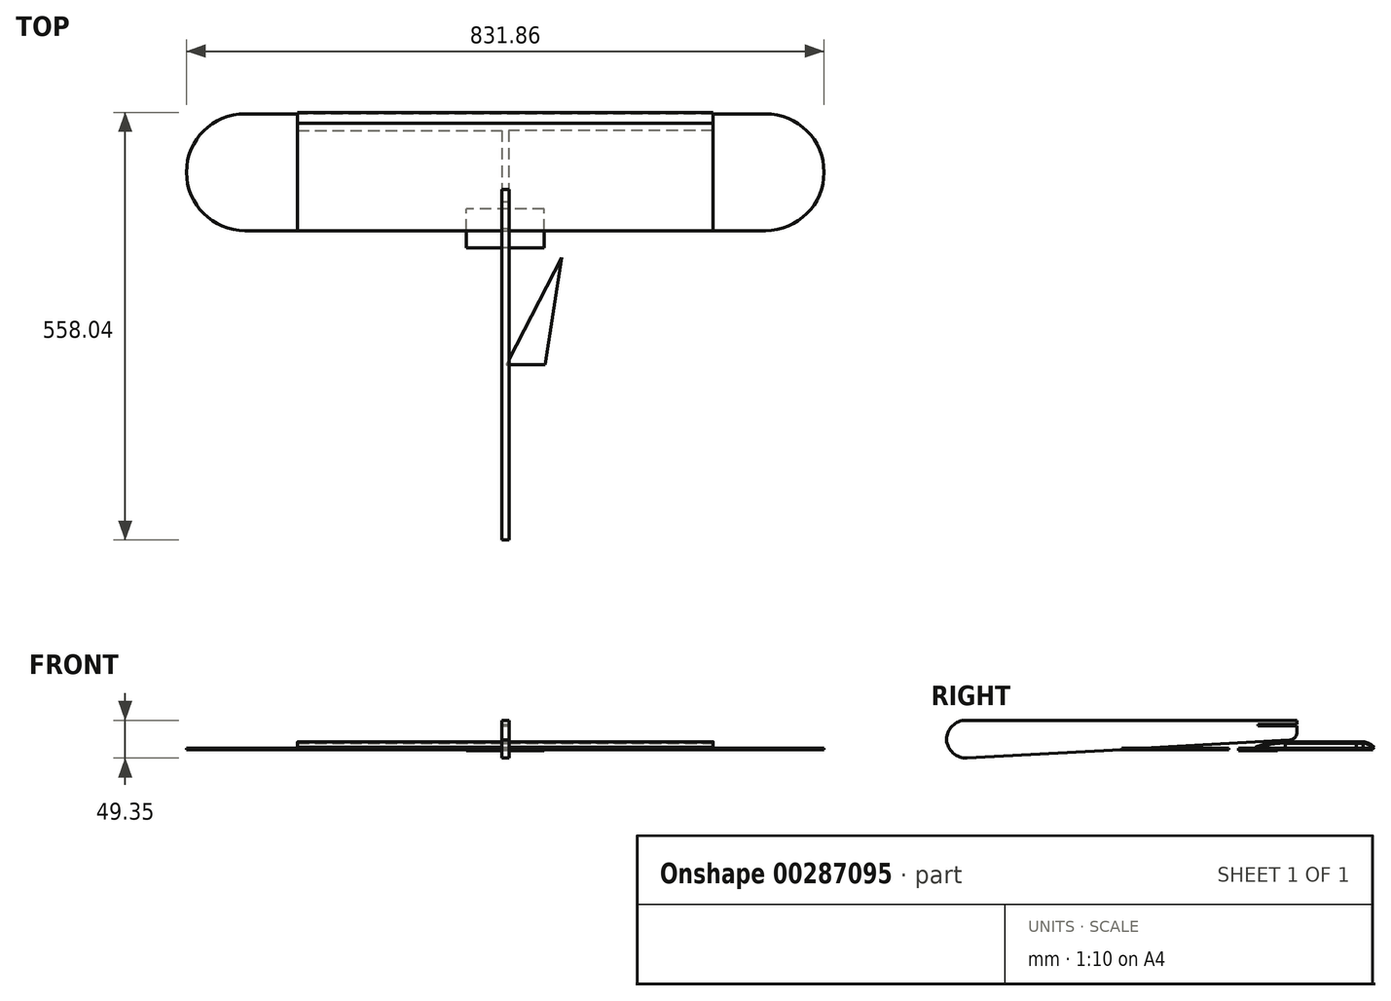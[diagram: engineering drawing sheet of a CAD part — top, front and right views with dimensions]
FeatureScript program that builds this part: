
annotation { "Feature Type Name" : "Feature", "Feature Type Description" : "" }
export const myFeature = defineFeature(function(context is Context, id is Id, definition is map)
    precondition{}
    {
        {
            var Q0;
            Q0=qCreatedBy(makeId("Front.planeOp"),FACE);
            var sketch = newSketch(context, id + "F0", { "sketchPlane" : qUnion([Q0])});
            skLineSegment(sketch, "E0.bottom", {"start": v(-75.02, 75.9) * mm, "end": v(-28.76, 75.9) * mm});
            skLineSegment(sketch, "E0.top", {"start": v(-75.02, 29.65) * mm, "end": v(-28.76, 29.65) * mm});
            skLineSegment(sketch, "E0.left", {"start": v(-75.02, 75.9) * mm, "end": v(-75.02, 29.65) * mm});
            skLineSegment(sketch, "E0.right", {"start": v(-28.76, 75.9) * mm, "end": v(-28.76, 29.65) * mm});
            skSolve(sketch);
        }
        {
            var Q0;
            Q0=qCreatedBy(makeId("Right.planeOp"),FACE);
            var sketch = newSketch(context, id + "F1", { "sketchPlane" : qUnion([Q0])});
            skLineSegment(sketch, "E1", {"start": v(0, 0) * mm, "end": v(0, 38.1) * mm});
            skLineSegment(sketch, "E2", {"start": v(0, 38.1) * mm, "end": v(228.6, 38.1) * mm});
            skLineSegment(sketch, "E3", {"start": v(228.6, 38.1) * mm, "end": v(228.6, 12.7) * mm});
            skLineSegment(sketch, "E4", {"start": v(0, 0) * mm, "end": v(228.6, 12.7) * mm});
            skSolve(sketch);
        }
        {
            var Q0;
            Q0=qCreatedBy(makeId("Top.planeOp"),FACE);
            var sketch = newSketch(context, id + "F2", { "sketchPlane" : qUnion([Q0])});
            skLineSegment(sketch, "E5", {"start": v(73.64, 139.7) * mm, "end": v(0.96, 0) * mm});
            skLineSegment(sketch, "E6", {"start": v(0.96, 0) * mm, "end": v(51.76, 0) * mm});
            skLineSegment(sketch, "E7", {"start": v(51.76, 0) * mm, "end": v(73.64, 139.7) * mm});
            skSolve(sketch);
        }
        {
            var Q0;
            Q0=qCreatedBy(makeId("Right.planeOp"),FACE);
            var sketch = newSketch(context, id + "F3", { "sketchPlane" : qUnion([Q0])});
            skLineSegment(sketch, "E8.bottom", {"start": v(152.4, 1.48) * mm, "end": v(203.2, 1.48) * mm});
            skLineSegment(sketch, "E8.top", {"start": v(152.4, -1.57) * mm, "end": v(203.2, -1.57) * mm});
            skLineSegment(sketch, "E8.left", {"start": v(152.4, 1.48) * mm, "end": v(152.4, -1.57) * mm});
            skLineSegment(sketch, "E8.right", {"start": v(203.2, 1.48) * mm, "end": v(203.2, -1.57) * mm});
            skSolve(sketch);
        }
        {
            var Q0;
            Q0=qCreatedBy(makeId("Right.planeOp"),FACE);
            var sketch = newSketch(context, id + "F4", { "sketchPlane" : qUnion([Q0])});
            skLineSegment(sketch, "E9", {"start": v(327.56, 0) * mm, "end": v(175.16, 0) * mm});
            skLineSegment(sketch, "E10.0", {"start": v(327.56, 1.65) * mm, "end": v(175.16, 1.65) * mm});
            skLineSegment(sketch, "E11", {"start": v(327.56, 1.65) * mm, "end": v(327.56, 0) * mm});
            skLineSegment(sketch, "E12", {"start": v(175.16, 0) * mm, "end": v(175.16, 1.65) * mm});
            skSolve(sketch);
        }
        {
            var Q0;
            Q0 = qSketchRegion(id + "F3", true);
            extrude(context, id + "F5", {"entities" : qUnion([Q0]), "endBound" : BoundingType.SYMMETRIC, "depth" : 101.6 * mm});
        }
        {
            var Q0;
            Q0=qCreatedBy(makeId("Right.planeOp"),FACE);
            var sketch = newSketch(context, id + "F6", { "sketchPlane" : qUnion([Q0])});
            skLineSegment(sketch, "E13.bottom", {"start": v(0, 38.1) * mm, "end": v(-228.6, 38.1) * mm});
            skLineSegment(sketch, "E13.left", {"start": v(0, 38.1) * mm, "end": v(0, 0) * mm});
            skLineSegment(sketch, "E13.right", {"start": v(-228.6, 38.1) * mm, "end": v(-228.6, -12.7) * mm});
            skLineSegment(sketch, "E14", {"start": v(0, 0) * mm, "end": v(-228.6, -12.7) * mm});
            skSolve(sketch);
        }
        {
            var Q0;
            Q0 = qSketchRegion(id + "F6", true);
            extrude(context, id + "F7", {"entities" : qUnion([Q0]), "endBound" : BoundingType.SYMMETRIC, "depth" : 9.52 * mm});
        }
        {
            var Q0;
            Q0 = qSketchRegion(id + "F4", true);
            extrude(context, id + "F8", {"entities" : qUnion([Q0]), "endBound" : BoundingType.SYMMETRIC, "depth" : 831.85 * mm});
        }
        {
            var Q0;
            Q0 = qSketchRegion(id + "F1", true);
            extrude(context, id + "F9", {"entities" : qUnion([Q0]), "endBound" : BoundingType.SYMMETRIC, "depth" : 9.52 * mm});
        }
        {
            var Q0;
            Q0 = qSketchRegion(id + "F4", true);
            extrude(context, id + "F10", {"entities" : qUnion([Q0]), "endBound" : BoundingType.SYMMETRIC, "depth" : 831.85 * mm});
        }
        {
            var Q0;
            Q0 = qSketchRegion(id + "F3", true);
            extrude(context, id + "F11", {"entities" : qUnion([Q0]), "endBound" : BoundingType.SYMMETRIC, "depth" : 101.6 * mm});
        }
        {
            var Q0;
            Q0=makeQuery(id+"F9.opExtrude","CAP_FACE",FACE,{"disambiguationData":[OSD([sQuery(id+"F1.wireOp",EDGE,"E1"),sQuery(id+"F1.wireOp",EDGE,"E2"),sQuery(id+"F1.wireOp",EDGE,"E3"),sQuery(id+"F1.wireOp",EDGE,"E4")])],"isStart":false});
            var sketch = newSketch(context, id + "F12", { "sketchPlane" : qUnion([Q0])});
            skLineSegment(sketch, "E15.bottom", {"start": v(228.6, 33.02) * mm, "end": v(177.8, 33.02) * mm});
            skLineSegment(sketch, "E15.top", {"start": v(228.6, 30.99) * mm, "end": v(177.8, 30.99) * mm});
            skLineSegment(sketch, "E15.left", {"start": v(228.6, 33.02) * mm, "end": v(228.6, 30.99) * mm});
            skLineSegment(sketch, "E15.right", {"start": v(177.8, 33.02) * mm, "end": v(177.8, 30.99) * mm});
            skSolve(sketch);
        }
        {
            var Q0;
            Q0 = qSketchRegion(id + "F12", true);
            extrude(context, id + "F13", {"entities" : qUnion([Q0]), "operationType" : NewBodyOperationType.REMOVE, "oppositeDirection" : true, "depth" : 25.4 * mm});
        }
        {
            var Q0;
            Q0=makeQuery(id+"F8.opExtrude","SWEPT_FACE",FACE,{"disambiguationData":[OSD([sQuery(id+"F4.wireOp",EDGE,"E10.0")])]});
            var sketch = newSketch(context, id + "F14", { "sketchPlane" : qUnion([Q0])});
            skLineSegment(sketch, "E16", {"start": v(0, 327.56) * mm, "end": v(0, 175.16) * mm, "construction": true});
            skLineSegment(sketch, "E17", {"start": v(0, 314.86) * mm, "end": v(271.15, 314.86) * mm});
            skLineSegment(sketch, "E18", {"start": v(271.15, 314.86) * mm, "end": v(271.15, 305.97) * mm});
            skLineSegment(sketch, "E19", {"start": v(271.15, 305.97) * mm, "end": v(4.44, 305.97) * mm});
            skLineSegment(sketch, "E20", {"start": v(4.44, 305.97) * mm, "end": v(4.45, 213.26) * mm});
            skLineSegment(sketch, "E21", {"start": v(4.45, 213.26) * mm, "end": v(0, 213.26) * mm});
            skLineSegment(sketch, "E22.MirrorCS", {"start": v(0, 314.86) * mm, "end": v(-271.15, 314.86) * mm});
            skLineSegment(sketch, "E23.MirrorCS", {"start": v(-271.15, 305.97) * mm, "end": v(-4.45, 305.97) * mm});
            skLineSegment(sketch, "E24.MirrorCS", {"start": v(-4.45, 305.97) * mm, "end": v(-4.44, 213.26) * mm});
            skLineSegment(sketch, "E25.MirrorCS", {"start": v(-271.15, 314.86) * mm, "end": v(-271.15, 305.97) * mm});
            skLineSegment(sketch, "E26.MirrorCS", {"start": v(-4.44, 213.26) * mm, "end": v(0, 213.26) * mm});
            skSolve(sketch);
        }
        {
            var Q0;
            Q0 = qSketchRegion(id + "F14", true);
            extrude(context, id + "F15", {"entities" : qUnion([Q0]), "operationType" : NewBodyOperationType.ADD, "depth" : 6.35 * mm});
        }
        {
            var Q0;
            Q0 = qSketchRegion(id + "F2", true);
            var Q1;
            Q1 = qConstructionFilter(qBodyType(qCreatedBy(id + "F2" ,EDGE), BodyType.WIRE), ConstructionObject.NO);
            extrude(context, id + "F16", {"entities" : qUnion([Q0]), "surfaceEntities" : qUnion([Q1]), "depth" : 1.52 * mm});
        }
        {
            var Q0;
            Q0=makeQuery(id+"F15.opExtrude","SWEPT_FACE",FACE,{"disambiguationData":[OSD([sQuery(id+"F14.wireOp",EDGE,"E24.MirrorCS")])]});
            cPlane(context, id + "F17", {"entities" : qUnion([Q0]), "cplaneType" : CPlaneType.OFFSET, "offset" : 4.44 * mm, "oppositeDirection" : true, "width" : 152.4 * mm, "height" : 152.4 * mm});
        }
        {
            var Q0;
            Q0=makeQuery(id+"F7.opExtrude","SWEPT_EDGE",EDGE,{"disambiguationData":[OSD([sQuery(id+"F6.wireOp",EDGE,"E13.bottom"),sQuery(id+"F6.wireOp",EDGE,"E13.right")])]});
            fillet(context, id + "F18", {"entities" : qUnion([Q0]), "radius" : 25.4 * mm, "tangentPropagation" : true, "allowEdgeOverflow" : false});
        }
        {
            var Q0;
            Q0=qCreatedBy(makeId("Right.planeOp"),FACE);
            var sketch = newSketch(context, id + "F19", { "sketchPlane" : qUnion([Q0])});
            skLineSegment(sketch, "E27.bottom", {"start": v(0, 33.02) * mm, "end": v(6.35, 33.02) * mm});
            skLineSegment(sketch, "E27.top", {"start": v(0, 26.67) * mm, "end": v(6.35, 26.67) * mm});
            skLineSegment(sketch, "E27.left", {"start": v(0, 33.02) * mm, "end": v(0, 26.67) * mm});
            skLineSegment(sketch, "E27.right", {"start": v(6.35, 33.02) * mm, "end": v(6.35, 26.67) * mm});
            skLineSegment(sketch, "E28.bottom", {"start": v(0, 21.59) * mm, "end": v(6.3, 21.59) * mm});
            skLineSegment(sketch, "E28.top", {"start": v(0, 15.24) * mm, "end": v(6.3, 15.24) * mm});
            skLineSegment(sketch, "E28.left", {"start": v(0, 21.59) * mm, "end": v(0, 15.24) * mm});
            skLineSegment(sketch, "E28.right", {"start": v(6.3, 21.59) * mm, "end": v(6.3, 15.24) * mm});
            skLineSegment(sketch, "E29.bottom", {"start": v(0, 10.16) * mm, "end": v(6.35, 10.16) * mm});
            skLineSegment(sketch, "E29.top", {"start": v(0, 3.8) * mm, "end": v(6.35, 3.8) * mm});
            skLineSegment(sketch, "E29.left", {"start": v(0, 10.16) * mm, "end": v(0, 3.8) * mm});
            skLineSegment(sketch, "E29.right", {"start": v(6.35, 10.16) * mm, "end": v(6.35, 3.8) * mm});
            skSolve(sketch);
        }
        {
            var Q0;
            Q0=makeQuery(id+"F7.opExtrude","SWEPT_EDGE",EDGE,{"disambiguationData":[OSD([sQuery(id+"F6.wireOp",EDGE,"E13.right"),sQuery(id+"F6.wireOp",EDGE,"E14")])]});
            fillet(context, id + "F20", {"entities" : qUnion([Q0]), "radius" : 25.4 * mm, "tangentPropagation" : true, "allowEdgeOverflow" : false});
        }
        {
            var Q0;
            Q0 = qSketchRegion(id + "F19", true);
            extrude(context, id + "F21", {"entities" : qUnion([Q0]), "operationType" : NewBodyOperationType.REMOVE, "endBound" : BoundingType.SYMMETRIC, "oppositeDirection" : true, "depth" : 25.4 * mm});
        }
        {
            var Q0;
            Q0=qCreatedBy(id+"F17.planeOp",FACE);
            var sketch = newSketch(context, id + "F22", { "sketchPlane" : qUnion([Q0])});
            skArc(sketch, "E30", {"start": v(-315.15, 8.44) * mm, "mid": v(-322.23, 6.14) * mm, "end": v(-328.28, 1.8) * mm});
            skLineSegment(sketch, "E31", {"start": v(-315.15, 8.44) * mm, "end": v(-212.82, 8.44) * mm});
            skArc(sketch, "E32", {"start": v(-175.35, 1.6) * mm, "mid": v(-193.78, 6.72) * mm, "end": v(-212.82, 8.44) * mm});
            skArc(sketch, "E33.0", {"start": v(-315.28, 10.09) * mm, "mid": v(-322.92, 7.64) * mm, "end": v(-329.44, 2.98) * mm});
            skLineSegment(sketch, "E33.1", {"start": v(-315.28, 10.09) * mm, "end": v(-212.82, 10.09) * mm});
            skArc(sketch, "E33.2", {"start": v(-174.76, 3.15) * mm, "mid": v(-193.48, 8.34) * mm, "end": v(-212.82, 10.09) * mm});
            skLineSegment(sketch, "E34", {"start": v(-328.28, 1.8) * mm, "end": v(-329.44, 2.98) * mm});
            skLineSegment(sketch, "E35", {"start": v(-175.35, 1.6) * mm, "end": v(-174.76, 3.15) * mm});
            skSolve(sketch);
        }
        {
            var Q0;
            Q0 = qSketchRegion(id + "F22", true);
            var Q1;
            Q1=makeQuery(id+"F15.opExtrude","SWEPT_FACE",FACE,{"disambiguationData":[OSD([sQuery(id+"F14.wireOp",EDGE,"E25.MirrorCS")])]});
            var Q2;
            Q2=makeQuery(id+"F15.opExtrude","SWEPT_FACE",FACE,{"disambiguationData":[OSD([sQuery(id+"F14.wireOp",EDGE,"E18")])]});
            extrude(context, id + "F23", {"entities" : qUnion([Q0]), "endBound" : BoundingType.UP_TO_SURFACE, "endBoundEntityFace" : qUnion([Q1]), "depth" : 635 * mm, "hasSecondDirection" : true, "secondDirectionBound" : SecondDirectionBoundingType.UP_TO_SURFACE, "secondDirectionOppositeDirection" : true, "secondDirectionBoundEntityFace" : qUnion([Q2]), "secondDirectionDepth" : 25.4 * mm});
        }
        {
            var Q0;
            Q0=qCreatedBy(makeId("Right.planeOp"),FACE);
            var sketch = newSketch(context, id + "F24", { "sketchPlane" : qUnion([Q0])});
            skLineSegment(sketch, "E36", {"start": v(0, 21.59) * mm, "end": v(6.3, 21.59) * mm});
            skLineSegment(sketch, "E37", {"start": v(6.3, 21.59) * mm, "end": v(6.3, 15.24) * mm});
            skLineSegment(sketch, "E38", {"start": v(0, 33.02) * mm, "end": v(6.35, 33.02) * mm});
            skLineSegment(sketch, "E39", {"start": v(6.35, 33.02) * mm, "end": v(6.35, 26.67) * mm});
            skLineSegment(sketch, "E40", {"start": v(6.35, 26.67) * mm, "end": v(0, 26.67) * mm});
            skLineSegment(sketch, "E41", {"start": v(0, 26.67) * mm, "end": v(0, 33.02) * mm});
            skLineSegment(sketch, "E42", {"start": v(0, 15.24) * mm, "end": v(0, 21.59) * mm});
            skLineSegment(sketch, "E43.bottom", {"start": v(0, 10.16) * mm, "end": v(6.35, 10.16) * mm});
            skLineSegment(sketch, "E43.top", {"start": v(0, 3.8) * mm, "end": v(6.35, 3.8) * mm});
            skLineSegment(sketch, "E43.left", {"start": v(0, 10.16) * mm, "end": v(0, 3.8) * mm});
            skLineSegment(sketch, "E43.right", {"start": v(6.35, 10.16) * mm, "end": v(6.35, 3.8) * mm});
            skLineSegment(sketch, "E44", {"start": v(0, 15.24) * mm, "end": v(6.3, 15.24) * mm});
            skSolve(sketch);
        }
        {
            var Q0;
            Q0=makeQuery(id+"F9.opExtrude","SWEPT_EDGE",EDGE,{"disambiguationData":[OSD([sQuery(id+"F1.wireOp",EDGE,"E3"),sQuery(id+"F1.wireOp",EDGE,"E4")])]});
            fillet(context, id + "F25", {"entities" : qUnion([Q0]), "radius" : 10.16 * mm, "tangentPropagation" : true, "allowEdgeOverflow" : false});
        }
        {
            var Q0;
            Q0 = qSketchRegion(id + "F24", true);
            extrude(context, id + "F26", {"entities" : qUnion([Q0]), "operationType" : NewBodyOperationType.ADD, "endBound" : BoundingType.SYMMETRIC, "depth" : 9.52 * mm});
        }
        {
            var Q0;
            Q0=makeQuery(id+"F8.opExtrude","CAP_EDGE",EDGE,{"disambiguationData":[OSD([sQuery(id+"F4.wireOp",EDGE,"E11")])],"isStart":false});
            var Q1;
            Q1=makeQuery(id+"F8.opExtrude","CAP_EDGE",EDGE,{"disambiguationData":[OSD([sQuery(id+"F4.wireOp",EDGE,"E12")])],"isStart":false});
            var Q2;
            Q2=makeQuery(id+"F8.opExtrude","CAP_EDGE",EDGE,{"disambiguationData":[OSD([sQuery(id+"F4.wireOp",EDGE,"E12")])],"isStart":true});
            var Q3;
            Q3=makeQuery(id+"F8.opExtrude","CAP_EDGE",EDGE,{"disambiguationData":[OSD([sQuery(id+"F4.wireOp",EDGE,"E11")])],"isStart":true});
            fillet(context, id + "F27", {"entities" : qUnion([Q0, Q1, Q2, Q3]), "radius" : 76.2 * mm, "tangentPropagation" : true, "allowEdgeOverflow" : false});
        }
    });
